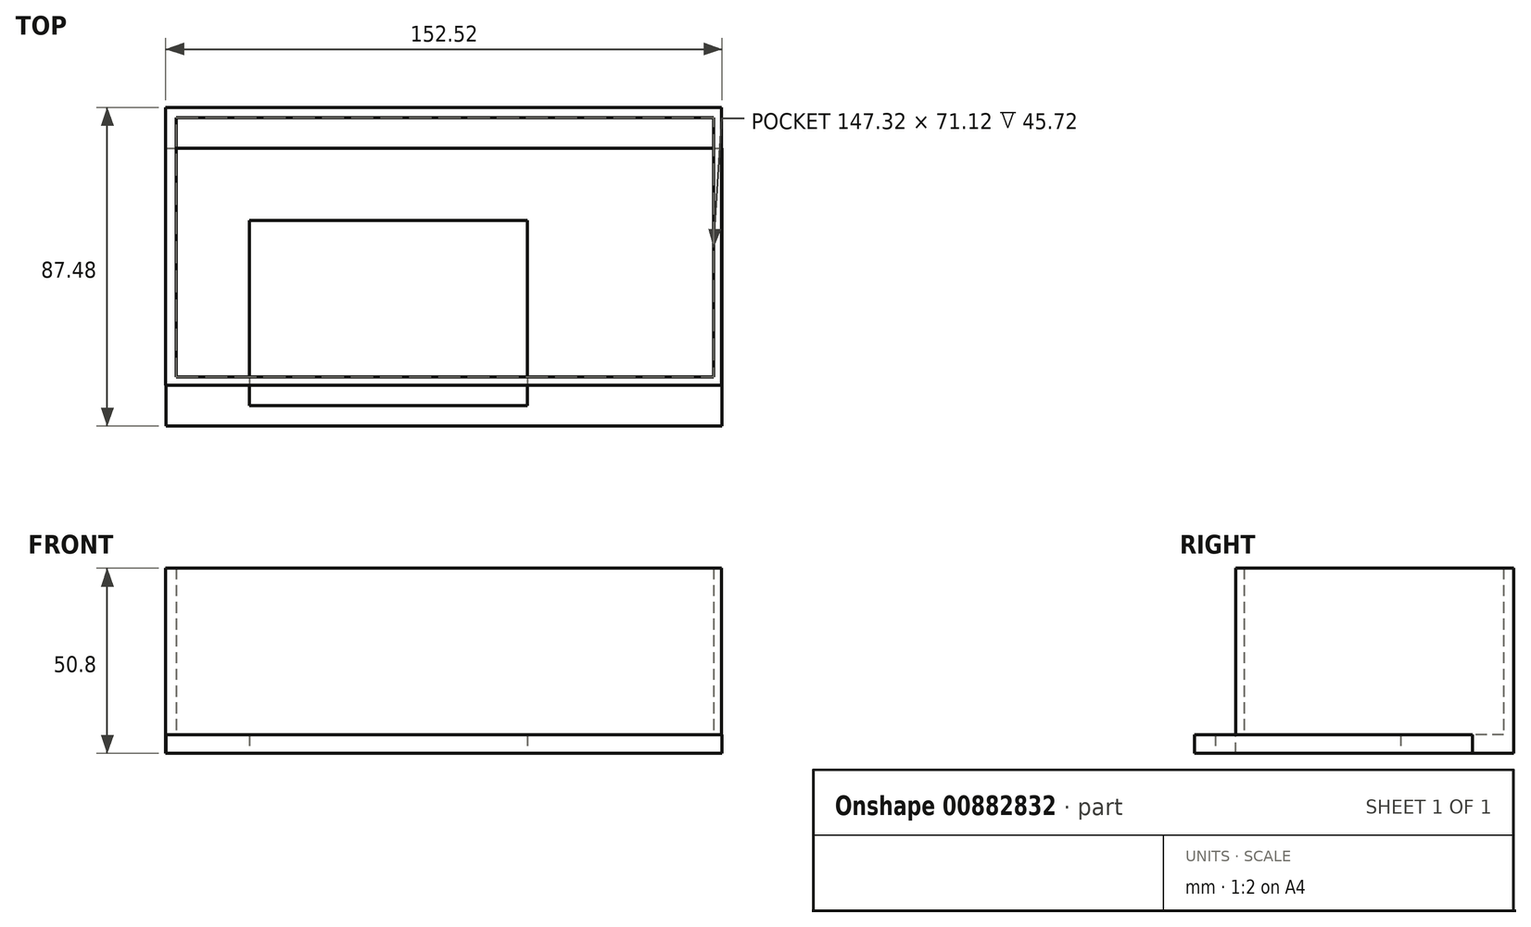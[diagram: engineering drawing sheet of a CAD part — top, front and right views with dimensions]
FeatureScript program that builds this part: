
annotation { "Feature Type Name" : "Feature", "Feature Type Description" : "" }
export const myFeature = defineFeature(function(context is Context, id is Id, definition is map)
    precondition{}
    {
        {
            var Q0;
            Q0=qCreatedBy(makeId("Top.planeOp"),FACE);
            var sketch = newSketch(context, id + "F0", { "sketchPlane" : qUnion([Q0])});
            skLineSegment(sketch, "E0.bottom", {"start": v(-75.91, 38.2) * mm, "end": v(76.49, 38.2) * mm});
            skLineSegment(sketch, "E0.top", {"start": v(-75.91, -38) * mm, "end": v(76.49, -38) * mm});
            skLineSegment(sketch, "E0.left", {"start": v(-75.91, 38.2) * mm, "end": v(-75.91, -38) * mm});
            skLineSegment(sketch, "E0.right", {"start": v(76.49, 38.2) * mm, "end": v(76.49, -38) * mm});
            skLineSegment(sketch, "E1.bottom", {"start": v(-73.09, 35.37) * mm, "end": v(74.23, 35.37) * mm});
            skLineSegment(sketch, "E1.top", {"start": v(-73.09, -35.75) * mm, "end": v(74.23, -35.75) * mm});
            skLineSegment(sketch, "E1.left", {"start": v(-73.09, 35.37) * mm, "end": v(-73.09, -35.75) * mm});
            skLineSegment(sketch, "E1.right", {"start": v(74.23, 35.37) * mm, "end": v(74.23, -35.75) * mm});
            skSolve(sketch);
        }
        {
            var Q0;
            Q0=makeQuery(id+"F0.imprint","IMPRINT",FACE,{"disambiguationData":[TD([[makeQuery(id+"F0.imprint","IMPRINT",EDGE,{"derivedFrom":sQuery(id+"F0.wireOp",EDGE,"E0.bottom")}),-1.0]])]});
            extrude(context, id + "F1", {"entities" : qUnion([Q0]), "depth" : 50.8 * mm, "offsetDistance" : 25.4 * mm});
        }
        {
            var Q0;
            Q0=makeQuery(id+"F0.imprint","IMPRINT",FACE,{"disambiguationData":[TD([[makeQuery(id+"F0.imprint","IMPRINT",EDGE,{"derivedFrom":sQuery(id+"F0.wireOp",EDGE,"E1.bottom")}),-1.0]])]});
            extrude(context, id + "F2", {"entities" : qUnion([Q0]), "operationType" : NewBodyOperationType.ADD, "depth" : 5.08 * mm, "offsetDistance" : 25.4 * mm});
        }
        {
            var Q0;
            Q0=qCreatedBy(makeId("Top.planeOp"),FACE);
            var sketch = newSketch(context, id + "F3", { "sketchPlane" : qUnion([Q0])});
            skLineSegment(sketch, "E2.bottom", {"start": v(-75.79, 26.9) * mm, "end": v(76.61, 26.9) * mm});
            skLineSegment(sketch, "E2.top", {"start": v(-75.79, -49.3) * mm, "end": v(76.61, -49.3) * mm});
            skLineSegment(sketch, "E2.left", {"start": v(-75.79, 26.9) * mm, "end": v(-75.79, -49.3) * mm});
            skLineSegment(sketch, "E2.right", {"start": v(76.61, 26.9) * mm, "end": v(76.61, -49.3) * mm});
            skLineSegment(sketch, "E3.bottom", {"start": v(-72.96, 24.08) * mm, "end": v(74.36, 24.08) * mm});
            skLineSegment(sketch, "E3.top", {"start": v(-72.96, -47.04) * mm, "end": v(74.36, -47.04) * mm});
            skLineSegment(sketch, "E3.left", {"start": v(-72.96, 24.08) * mm, "end": v(-72.96, -47.04) * mm});
            skLineSegment(sketch, "E3.right", {"start": v(74.36, 24.08) * mm, "end": v(74.36, -47.04) * mm});
            skSolve(sketch);
        }
        {
            var Q0;
            Q0=makeQuery(id+"F3.imprint","IMPRINT",FACE,{"disambiguationData":[TD([[makeQuery(id+"F3.imprint","IMPRINT",EDGE,{"derivedFrom":sQuery(id+"F3.wireOp",EDGE,"E2.bottom")}),-1.0]])]});
            var Q1;
            Q1=makeQuery(id+"F3.imprint","IMPRINT",FACE,{"disambiguationData":[TD([[makeQuery(id+"F3.imprint","IMPRINT",EDGE,{"derivedFrom":sQuery(id+"F3.wireOp",EDGE,"E3.bottom")}),-1.0]])]});
            extrude(context, id + "F4", {"entities" : qUnion([Q0, Q1]), "depth" : 5.08 * mm, "offsetDistance" : 25.4 * mm});
        }
        {
            var Q0;
            Q0=qCreatedBy(makeId("Top.planeOp"),FACE);
            var sketch = newSketch(context, id + "F5", { "sketchPlane" : qUnion([Q0])});
            skLineSegment(sketch, "E4.bottom", {"start": v(-53, 7.15) * mm, "end": v(23.2, 7.15) * mm});
            skLineSegment(sketch, "E4.top", {"start": v(-53, -43.65) * mm, "end": v(23.2, -43.65) * mm});
            skLineSegment(sketch, "E4.left", {"start": v(-53, 7.15) * mm, "end": v(-53, -43.65) * mm});
            skLineSegment(sketch, "E4.right", {"start": v(23.2, 7.15) * mm, "end": v(23.2, -43.65) * mm});
            skSolve(sketch);
        }
        {
            var Q0;
            Q0=makeQuery(id+"F5.imprint","IMPRINT",FACE,{"disambiguationData":[TD([[makeQuery(id+"F5.imprint","IMPRINT",EDGE,{"derivedFrom":sQuery(id+"F5.wireOp",EDGE,"E4.bottom")}),-1.0]])]});
            extrude(context, id + "F6", {"entities" : qUnion([Q0]), "depth" : 5.08 * mm, "offsetDistance" : 25.4 * mm});
        }
    });
